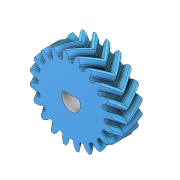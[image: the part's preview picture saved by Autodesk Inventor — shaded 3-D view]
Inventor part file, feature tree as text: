
AUTODESK INVENTOR PART (.ipt)
format: ipt  version: 2020.3 (Build 243373000, 373)  size: 1,537,536 bytes
history: native  units: mm
features: extrude x1, sketch x1, imported_body x1
ambient origin geometry x8: Origin, YZ Plane, XZ Plane, XY Plane, X Axis, Y Axis, Z Axis, Center Point
bodies: Solid1 (feature_tree)
feature tree (3):
  extrude  "Extrusion1"  [1 undecoded]
  sketch  "Sketch1"  dims[d0=86.0mm d1=0.0mm]
  imported_body  "Base1"
note: 1 required parameter value undecoded (feature->parameter linkage not recoverable at this tier; creation-order binding heuristic only, values carry confidence <= 0.55)
